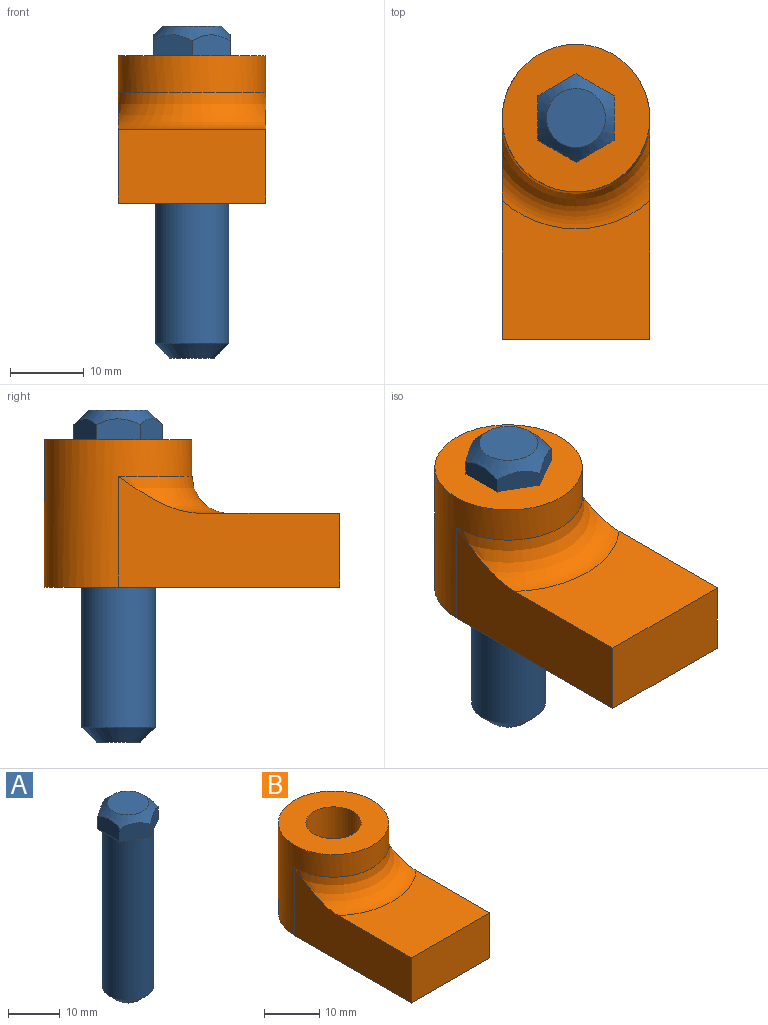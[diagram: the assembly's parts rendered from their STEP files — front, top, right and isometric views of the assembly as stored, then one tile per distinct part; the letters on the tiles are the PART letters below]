
ASSEMBLY  parts=2 mates=1
PART A: 12 faces, bbox 12x12x45 mm
  f0: plane 12x10.39mm, normal (0,0,-1), area 15mm2, adj f3,f4,f5,f6,f7,f8,f9
  f1: cone r=4mm half-angle=45deg, axis (0,0,-1), area 61.2mm2, adj f2,f3,f4,f5,f6,f7,f8
  f2: plane 8x8mm, normal (0,0,1), area 50.3mm2, adj f1
  f3: plane 5.2x3.81mm, normal (0.5,0.87,0), area 21.2mm2, adj f0,f1,f7,f8
  f4: plane 5.2x3.81mm, normal (0.5,-0.87,0), area 21.2mm2, adj f0,f1,f6,f8
  f5: plane 6.01x3.8mm, normal (-1,0,0), area 21.2mm2, adj f0,f1,f6,f7
  f6: plane 5.2x3.81mm, normal (-0.5,-0.87,0), area 21.2mm2, adj f0,f1,f4,f5
  f7: plane 5.2x3.81mm, normal (-0.5,0.87,0), area 21.2mm2, adj f0,f1,f3,f5
  f8: plane 6.01x3.8mm, normal (1,0,0), area 21.2mm2, adj f0,f1,f3,f4
  f9: cylinder r=5mm len=38mm, axis (0,0,1), area 1193.8mm2, adj f0,f11
  f10: plane 6x6mm, normal (0,0,-1), area 28.3mm2, adj f11
  f11: cone r=5mm half-angle=45deg, axis (0,0,1), area 71.1mm2, adj f9,f10
PART B: 9 faces, bbox 40.2x40x20 mm
  f0: cylinder r=10mm len=20mm, axis (0,0,-1), area 785.4mm2, adj f1,f3,f5,f6,f8
  f1: plane 30x15mm, normal (-1,0,0), area 320.4mm2, adj f0,f2,f4,f5,f8
  f2: plane 20x10mm, normal (0,-1,0), area 200mm2, adj f1,f3,f4,f5
  f3: plane 30x15mm, normal (1,0,0), area 320.4mm2, adj f0,f2,f4,f5,f8
  f4: plane 20x18.82mm, normal (0,0,1), area 324mm2, adj f1,f2,f3,f8
  f5: plane 40x20mm, normal (0,0,-1), area 678.5mm2, adj f0,f1,f2,f3,f7
  f6: plane 20x20mm, normal (0,0,1), area 235.6mm2, adj f0,f7
  f7: cylinder r=5mm len=20mm, axis (0,0,1), area 628.3mm2, adj f5,f6
  f8: torus R=15mm, axis (0,0,1), area 196.9mm2, adj f0,f1,f3,f4
PLACE A t=(0,0,19)mm
PLACE B at identity fixed
MATE cylindrical A.f9 <-> B.f7  axis (0,0,1) through (0,0,19)mm
